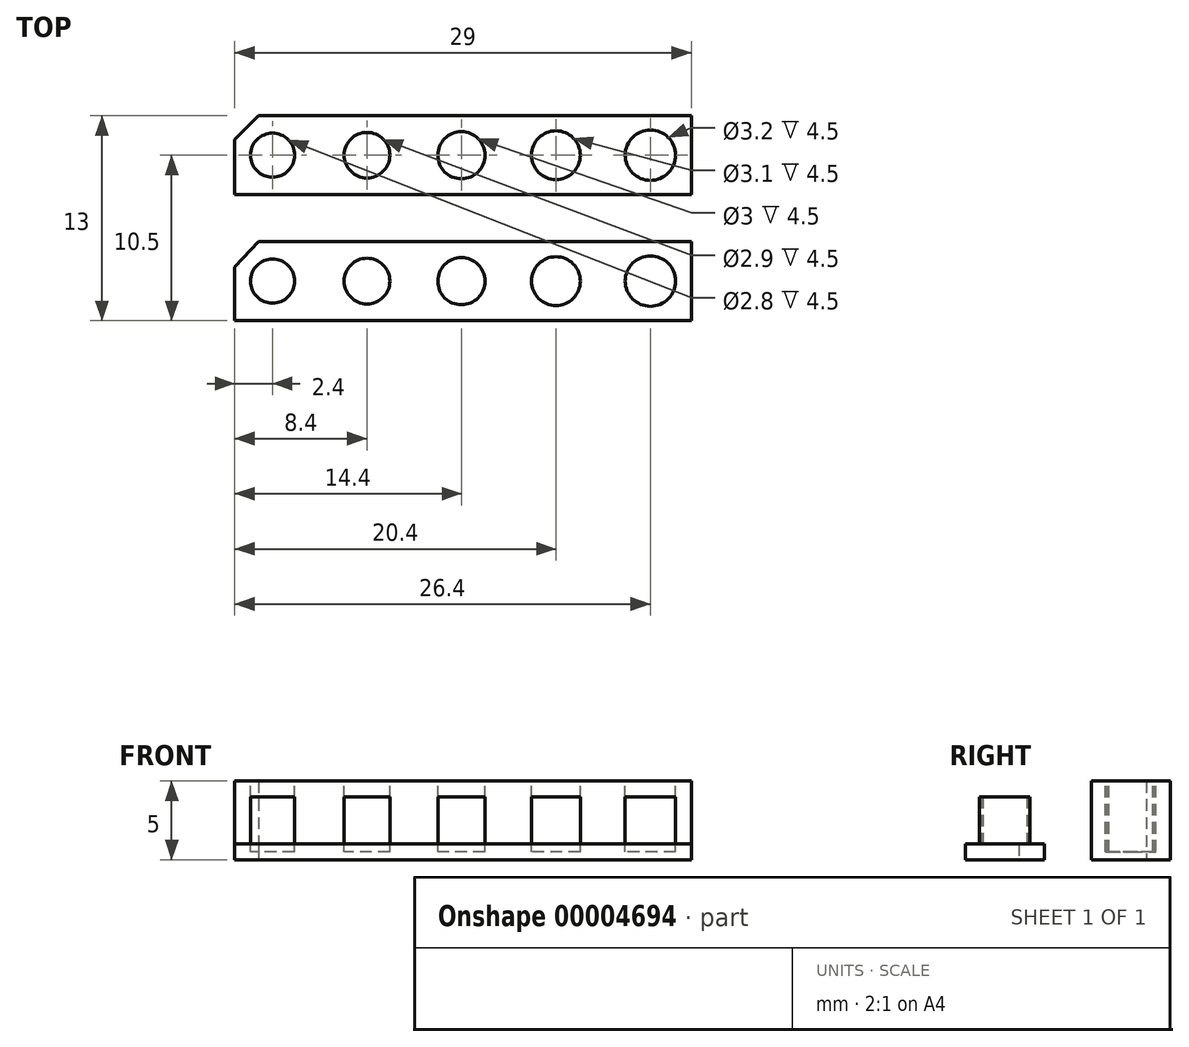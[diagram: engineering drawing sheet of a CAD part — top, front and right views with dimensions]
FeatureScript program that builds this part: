
annotation { "Feature Type Name" : "Feature", "Feature Type Description" : "" }
export const myFeature = defineFeature(function(context is Context, id is Id, definition is map)
    precondition{}
    {
        {
            var Q0;
            Q0=qCreatedBy(makeId("Top.planeOp"),FACE);
            var sketch = newSketch(context, id + "F0", { "sketchPlane" : qUnion([Q0])});
            skLineSegment(sketch, "E0.bottom", {"start": v(0, 0) * mm, "end": v(29, 0) * mm});
            skLineSegment(sketch, "E0.top", {"start": v(0, 5) * mm, "end": v(29, 5) * mm});
            skLineSegment(sketch, "E0.left", {"start": v(0, 0) * mm, "end": v(0, 5) * mm});
            skLineSegment(sketch, "E0.right", {"start": v(29, 0) * mm, "end": v(29, 5) * mm});
            skLineSegment(sketch, "E1", {"start": v(0, 3.4) * mm, "end": v(1.5, 5) * mm});
            skLineSegment(sketch, "E2", {"start": v(0, 2.5) * mm, "end": v(29, 2.5) * mm, "construction": true});
            skPoint(sketch, "E3", {"position": v(2.4, 2.5) * mm});
            skPoint(sketch, "E4.1.0.0", {"position": v(8.4, 2.5) * mm});
            skPoint(sketch, "E4.2.0.0", {"position": v(14.4, 2.5) * mm});
            skLineSegment(sketch, "E4.direction1", {"start": v(2.4, 2.5) * mm, "end": v(8.4, 2.5) * mm, "construction": true});
            skPoint(sketch, "E5.0.3.0", {"position": v(20.4, 2.5) * mm});
            skPoint(sketch, "E5.0.4.0", {"position": v(26.4, 2.5) * mm});
            skCircle(sketch, "E6", {"center": v(2.4, 2.5) * mm, "radius": 1.4 * mm});
            skCircle(sketch, "E7", {"center": v(8.4, 2.5) * mm, "radius": 1.45 * mm});
            skCircle(sketch, "E8", {"center": v(14.4, 2.5) * mm, "radius": 1.5 * mm});
            skCircle(sketch, "E9", {"center": v(20.4, 2.5) * mm, "radius": 1.55 * mm});
            skCircle(sketch, "E10", {"center": v(26.4, 2.5) * mm, "radius": 1.6 * mm});
            skSolve(sketch);
        }
        {
            var Q0;
            Q0=makeQuery(id+"F0.imprint","IMPRINT",FACE,{"disambiguationData":[TD([[makeQuery(id+"F0.imprint","IMPRINT",EDGE,{"derivedFrom":sQuery(id+"F0.wireOp",EDGE,"E7")}),1.0]])]});
            var Q1;
            Q1=makeQuery(id+"F0.imprint","IMPRINT",FACE,{"disambiguationData":[TD([[makeQuery(id+"F0.imprint","IMPRINT",EDGE,{"derivedFrom":sQuery(id+"F0.wireOp",EDGE,"E6")}),1.0]])]});
            var Q2;
            Q2=makeQuery(id+"F0.imprint","IMPRINT",FACE,{"disambiguationData":[TD([[makeQuery(id+"F0.imprint","IMPRINT",EDGE,{"derivedFrom":sQuery(id+"F0.wireOp",EDGE,"E9")}),1.0]])]});
            var Q3;
            Q3=makeQuery(id+"F0.imprint","IMPRINT",FACE,{"disambiguationData":[TD([[makeQuery(id+"F0.imprint","IMPRINT",EDGE,{"derivedFrom":sQuery(id+"F0.wireOp",EDGE,"E8")}),1.0]])]});
            var Q4;
            Q4=makeQuery(id+"F0.imprint","IMPRINT",FACE,{"disambiguationData":[TD([[makeQuery(id+"F0.imprint","IMPRINT",EDGE,{"derivedFrom":sQuery(id+"F0.wireOp",EDGE,"E10")}),1.0]])]});
            var Q5;
            {var subQ3=sQuery(id+"F0.wireOp",EDGE,"E0.bottom");Q5=makeQuery(id+"F0.imprint","IMPRINT",FACE,{"disambiguationData":[TD([[makeQuery(id+"F0.imprint","IMPRINT",EDGE,{"derivedFrom":subQ3}),1.0]])]});}
            extrude(context, id + "F1", {"entities" : qUnion([Q0, Q1, Q2, Q3, Q4, Q5]), "depth" : 1 * mm});
        }
        {
            var Q0;
            Q0=makeQuery(id+"F0.imprint","IMPRINT",FACE,{"disambiguationData":[TD([[makeQuery(id+"F0.imprint","IMPRINT",EDGE,{"derivedFrom":sQuery(id+"F0.wireOp",EDGE,"E6")}),1.0]])]});
            var Q1;
            Q1=makeQuery(id+"F0.imprint","IMPRINT",FACE,{"disambiguationData":[TD([[makeQuery(id+"F0.imprint","IMPRINT",EDGE,{"derivedFrom":sQuery(id+"F0.wireOp",EDGE,"E7")}),1.0]])]});
            var Q2;
            Q2=makeQuery(id+"F0.imprint","IMPRINT",FACE,{"disambiguationData":[TD([[makeQuery(id+"F0.imprint","IMPRINT",EDGE,{"derivedFrom":sQuery(id+"F0.wireOp",EDGE,"E8")}),1.0]])]});
            var Q3;
            Q3=makeQuery(id+"F0.imprint","IMPRINT",FACE,{"disambiguationData":[TD([[makeQuery(id+"F0.imprint","IMPRINT",EDGE,{"derivedFrom":sQuery(id+"F0.wireOp",EDGE,"E9")}),1.0]])]});
            var Q4;
            Q4=makeQuery(id+"F0.imprint","IMPRINT",FACE,{"disambiguationData":[TD([[makeQuery(id+"F0.imprint","IMPRINT",EDGE,{"derivedFrom":sQuery(id+"F0.wireOp",EDGE,"E10")}),1.0]])]});
            extrude(context, id + "F2", {"entities" : qUnion([Q0, Q1, Q2, Q3, Q4]), "operationType" : NewBodyOperationType.ADD, "depth" : 4 * mm});
        }
        {
            var Q0;
            Q0=qCreatedBy(makeId("Top.planeOp"),FACE);
            var sketch = newSketch(context, id + "F3", { "sketchPlane" : qUnion([Q0])});
            skLineSegment(sketch, "E11.bottom", {"start": v(0, 8) * mm, "end": v(29, 8) * mm});
            skLineSegment(sketch, "E11.top", {"start": v(0, 13) * mm, "end": v(29, 13) * mm});
            skLineSegment(sketch, "E11.left", {"start": v(0, 8) * mm, "end": v(0, 13) * mm});
            skLineSegment(sketch, "E11.right", {"start": v(29, 8) * mm, "end": v(29, 13) * mm});
            skLineSegment(sketch, "E12", {"start": v(0, 10.5) * mm, "end": v(29, 10.5) * mm, "construction": true});
            skLineSegment(sketch, "E13", {"start": v(0, 11.5) * mm, "end": v(1.5, 13) * mm});
            skSolve(sketch);
        }
        {
            var Q0;
            Q0=makeQuery(id+"F3.imprint","IMPRINT",FACE,{"disambiguationData":[TD([[makeQuery(id+"F3.imprint","IMPRINT",EDGE,{"derivedFrom":sQuery(id+"F3.wireOp",EDGE,"E11.bottom")}),1.0]])]});
            extrude(context, id + "F4", {"entities" : qUnion([Q0]), "depth" : 5 * mm});
        }
        {
            var Q0;
            Q0=makeQuery(id+"F4.opExtrude","CAP_FACE",FACE,{"disambiguationData":[OSD([sQuery(id+"F3.wireOp",EDGE,"E11.bottom"),sQuery(id+"F3.wireOp",EDGE,"E11.top"),sQuery(id+"F3.wireOp",EDGE,"E11.left"),sQuery(id+"F3.wireOp",EDGE,"E11.right")])],"isStart":false});
            var sketch = newSketch(context, id + "F5", { "sketchPlane" : qUnion([Q0])});
            skLineSegment(sketch, "E14", {"start": v(0, 10.5) * mm, "end": v(29, 10.5) * mm, "construction": true});
            skPoint(sketch, "E15", {"position": v(2.4, 10.5) * mm});
            skPoint(sketch, "E16.1.0.0", {"position": v(8.4, 10.5) * mm});
            skPoint(sketch, "E16.2.0.0", {"position": v(14.4, 10.5) * mm});
            skLineSegment(sketch, "E16.direction1", {"start": v(2.4, 10.5) * mm, "end": v(8.4, 10.5) * mm, "construction": true});
            skPoint(sketch, "E17.0.3.0", {"position": v(20.4, 10.5) * mm});
            skPoint(sketch, "E17.0.4.0", {"position": v(26.4, 10.5) * mm});
            skCircle(sketch, "E18", {"center": v(2.4, 10.5) * mm, "radius": 1.4 * mm});
            skCircle(sketch, "E19", {"center": v(8.4, 10.5) * mm, "radius": 1.45 * mm});
            skCircle(sketch, "E20", {"center": v(14.4, 10.5) * mm, "radius": 1.5 * mm});
            skCircle(sketch, "E21", {"center": v(20.4, 10.5) * mm, "radius": 1.55 * mm});
            skCircle(sketch, "E22", {"center": v(26.4, 10.5) * mm, "radius": 1.6 * mm});
            skSolve(sketch);
        }
        {
            var Q0;
            Q0=makeQuery(id+"F5.imprint","IMPRINT",FACE,{"disambiguationData":[TD([[makeQuery(id+"F5.imprint","IMPRINT",EDGE,{"derivedFrom":sQuery(id+"F5.wireOp",EDGE,"E18")}),1.0]])]});
            var Q1;
            Q1=makeQuery(id+"F5.imprint","IMPRINT",FACE,{"disambiguationData":[TD([[makeQuery(id+"F5.imprint","IMPRINT",EDGE,{"derivedFrom":sQuery(id+"F5.wireOp",EDGE,"E19")}),1.0]])]});
            var Q2;
            Q2=makeQuery(id+"F5.imprint","IMPRINT",FACE,{"disambiguationData":[TD([[makeQuery(id+"F5.imprint","IMPRINT",EDGE,{"derivedFrom":sQuery(id+"F5.wireOp",EDGE,"E20")}),1.0]])]});
            var Q3;
            Q3=makeQuery(id+"F5.imprint","IMPRINT",FACE,{"disambiguationData":[TD([[makeQuery(id+"F5.imprint","IMPRINT",EDGE,{"derivedFrom":sQuery(id+"F5.wireOp",EDGE,"E21")}),1.0]])]});
            var Q4;
            Q4=makeQuery(id+"F5.imprint","IMPRINT",FACE,{"disambiguationData":[TD([[makeQuery(id+"F5.imprint","IMPRINT",EDGE,{"derivedFrom":sQuery(id+"F5.wireOp",EDGE,"E22")}),1.0]])]});
            var Q5;
            Q5=makeQuery(id+"F5.imprint","IMPRINT",FACE,{"disambiguationData":[TD([[makeQuery(id+"F5.imprint","IMPRINT",EDGE,{"derivedFrom":sQuery(id+"F5.wireOp",EDGE,"E21")}),1.0]])]});
            extrude(context, id + "F6", {"entities" : qUnion([Q0, Q1, Q2, Q3, Q4, Q5]), "operationType" : NewBodyOperationType.REMOVE, "oppositeDirection" : true, "depth" : 4.5 * mm});
        }
    });
